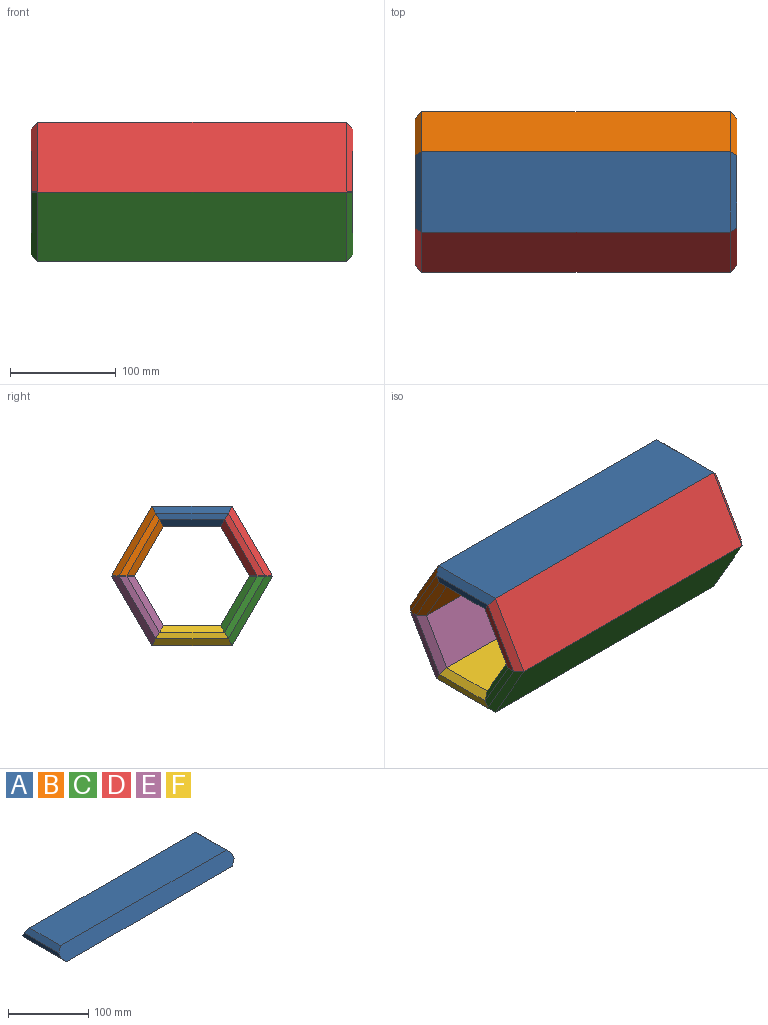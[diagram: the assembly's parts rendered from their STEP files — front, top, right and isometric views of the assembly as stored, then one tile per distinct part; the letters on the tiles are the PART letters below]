
ASSEMBLY  parts=6 mates=5
PART A: 10 faces, bbox 304.8x76.2x19.1 mm
  f0: plane 68.87x6.35mm, normal (-1,0,0), area 414mm2, adj f4,f5,f8,f9
  f1: plane 68.87x6.35mm, normal (1,0,0), area 414mm2, adj f4,f5,f6,f7
  f2: plane 292.1x54.2mm, normal (0,0,1), area 15832.7mm2, adj f4,f5,f7,f9
  f3: plane 292.1x76.2mm, normal (0,0,-1), area 22258mm2, adj f4,f5,f6,f8
  f4: plane 304.8x19.05mm, normal (0,0.87,0.5), area 6611.6mm2, adj f0,f1,f2,f3,f6,f7,f8,f9
  f5: plane 304.8x19.05mm, normal (0,-0.87,0.5), area 6611.6mm2, adj f0,f1,f2,f3,f6,f7,f8,f9
  f6: plane 76.2x6.35mm, normal (0.71,0,-0.71), area 651.4mm2, adj f1,f3,f4,f5
  f7: plane 61.54x6.35mm, normal (0.71,0,0.71), area 519.7mm2, adj f1,f2,f4,f5
  f8: plane 76.2x6.35mm, normal (-0.71,0,-0.71), area 651.4mm2, adj f0,f3,f4,f5
  f9: plane 61.54x6.35mm, normal (-0.71,0,0.71), area 519.7mm2, adj f0,f2,f4,f5
PART B: same geometry as A
PART C: same geometry as A
PART D: same geometry as A
PART E: same geometry as A
PART F: same geometry as A
PLACE A rot(axis=(-1,0,0),180deg) t=(-152.4,-38.1,112.93)mm
PLACE B rot(axis=(1,0,0),120deg) t=(-152.4,38.1,112.93)mm
PLACE C rot(axis=(-1,0,0),60deg) t=(-152.4,-38.1,-19.05)mm
PLACE D rot(axis=(-1,0,0),120deg) t=(-152.4,-76.2,46.94)mm
PLACE E rot(axis=(1,0,0),60deg) t=(-152.4,76.2,46.94)mm
PLACE F t=(-152.4,38.1,-19.05)mm
MATE fastened F.f5 <-> C.f4  axis (0,-0.87,0.5) through (0,-32.6,-9.52)mm
MATE fastened E.f4 <-> B.f5  axis (0,0,1) through (0,65.2,46.94)mm
MATE fastened C.f5 <-> D.f4  axis (0,0,1) through (0,-65.2,46.94)mm
MATE fastened D.f5 <-> A.f4  axis (0,0.87,0.5) through (0,-32.6,103.41)mm
MATE fastened F.f4 <-> E.f5  axis (0,0.87,0.5) through (0,32.6,-9.52)mm
